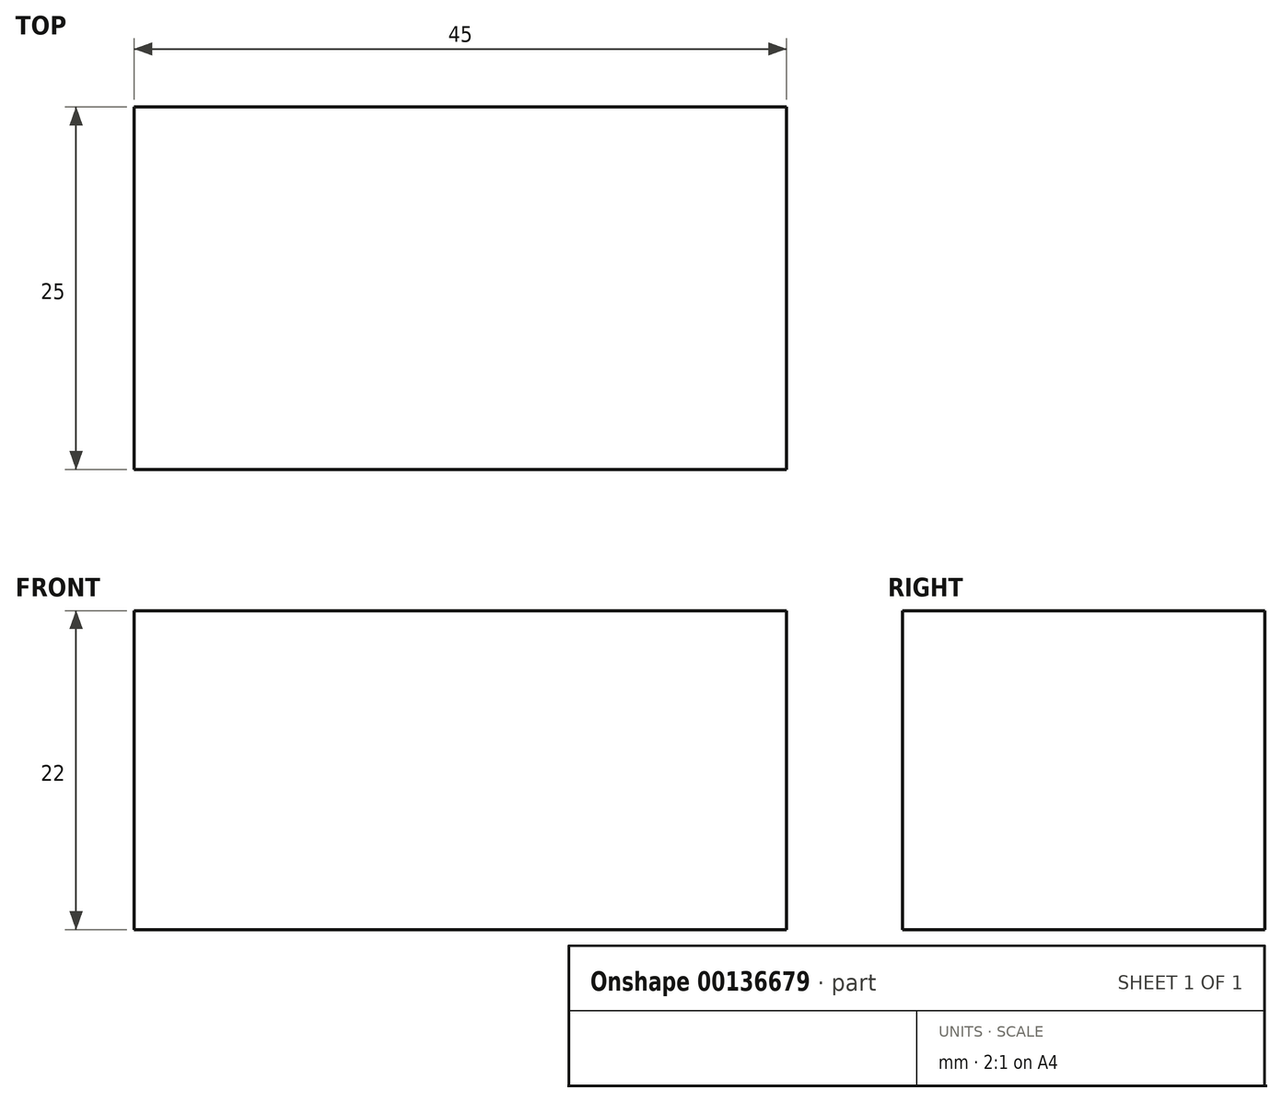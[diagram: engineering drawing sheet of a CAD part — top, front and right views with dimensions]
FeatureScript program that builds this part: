
annotation { "Feature Type Name" : "Feature", "Feature Type Description" : "" }
export const myFeature = defineFeature(function(context is Context, id is Id, definition is map)
    precondition{}
    {
        {
            var Q0;
            Q0=qCreatedBy(makeId("Top.planeOp"),FACE);
            var sketch = newSketch(context, id + "F0", { "sketchPlane" : qUnion([Q0])});
            skLineSegment(sketch, "E0.bottom", {"start": v(22.5, 12.5) * mm, "end": v(-22.5, 12.5) * mm});
            skLineSegment(sketch, "E0.top", {"start": v(22.5, -12.5) * mm, "end": v(-22.5, -12.5) * mm});
            skLineSegment(sketch, "E0.left", {"start": v(22.5, 12.5) * mm, "end": v(22.5, -12.5) * mm});
            skLineSegment(sketch, "E0.right", {"start": v(-22.5, 12.5) * mm, "end": v(-22.5, -12.5) * mm});
            skPoint(sketch, "E0.middle", {"position": v(0, 0) * mm});
            skSolve(sketch);
        }
        {
            var Q0;
            Q0=makeQuery(id+"F0.imprint","IMPRINT",FACE,{"disambiguationData":[TD([[makeQuery(id+"F0.imprint","IMPRINT",EDGE,{"derivedFrom":sQuery(id+"F0.wireOp",EDGE,"E0.bottom")}),1.0]])]});
            extrude(context, id + "F1", {"entities" : qUnion([Q0]), "depth" : 22 * mm});
        }
    });
